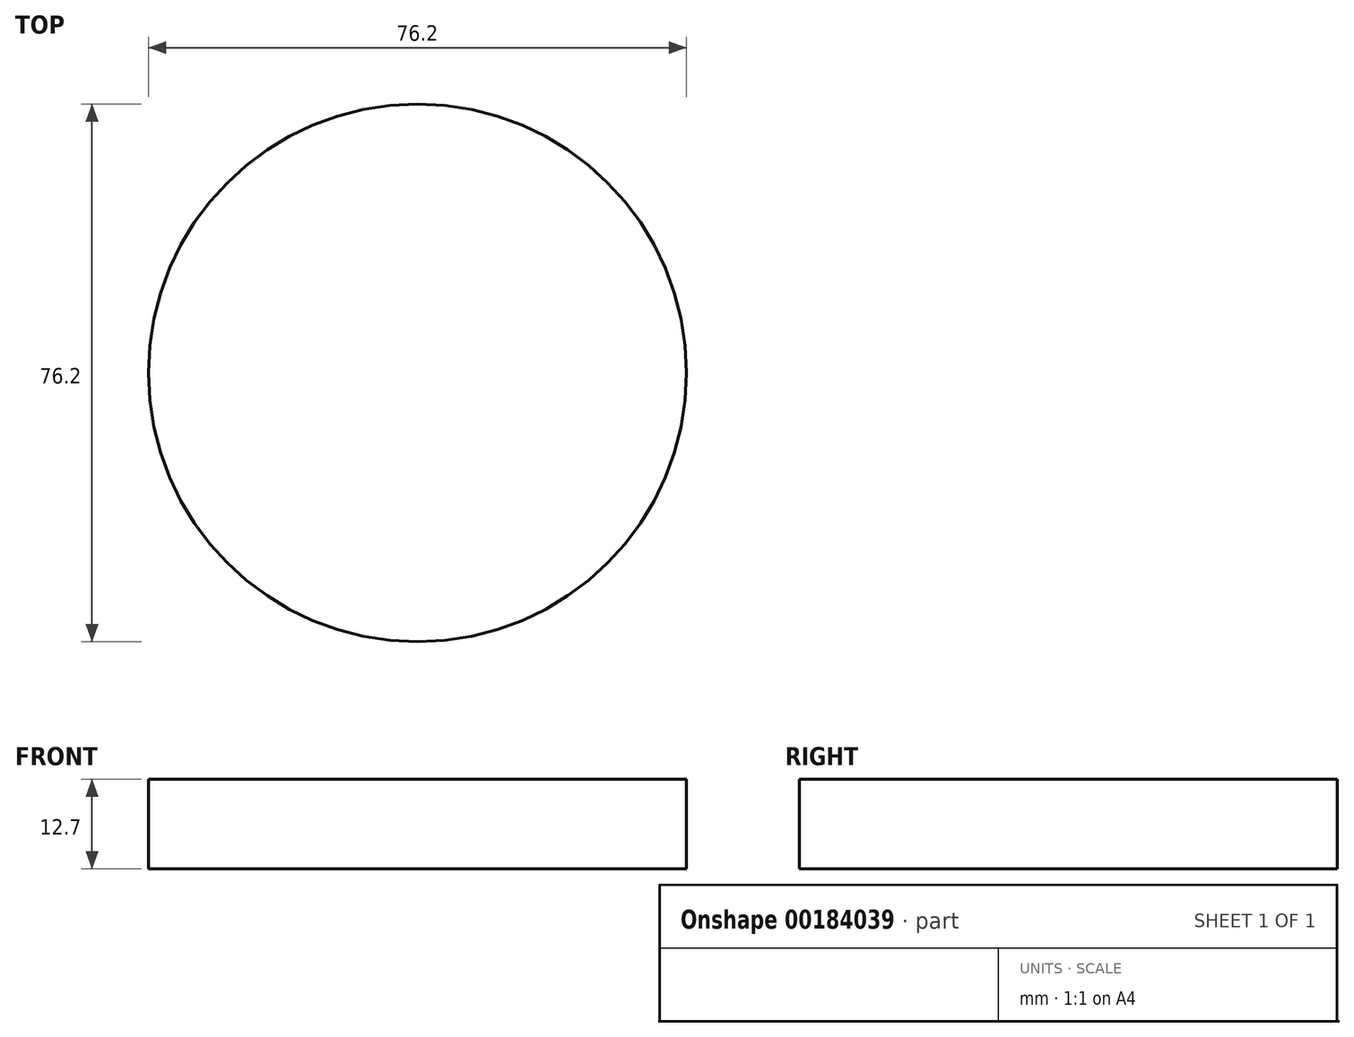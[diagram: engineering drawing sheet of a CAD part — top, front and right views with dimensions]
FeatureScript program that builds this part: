
annotation { "Feature Type Name" : "Feature", "Feature Type Description" : "" }
export const myFeature = defineFeature(function(context is Context, id is Id, definition is map)
    precondition{}
    {
        {
            var Q0;
            Q0=qCreatedBy(makeId("Top.planeOp"),FACE);
            var sketch = newSketch(context, id + "F0", { "sketchPlane" : qUnion([Q0])});
            skCircle(sketch, "E0", {"center": v(0, 0) * mm, "radius": 38.1 * mm});
            skSolve(sketch);
        }
        {
            var Q0;
            Q0 = qSketchRegion(id + "F0", true);
            extrude(context, id + "F1", {"entities" : qUnion([Q0]), "depth" : 12.7 * mm});
        }
    });
